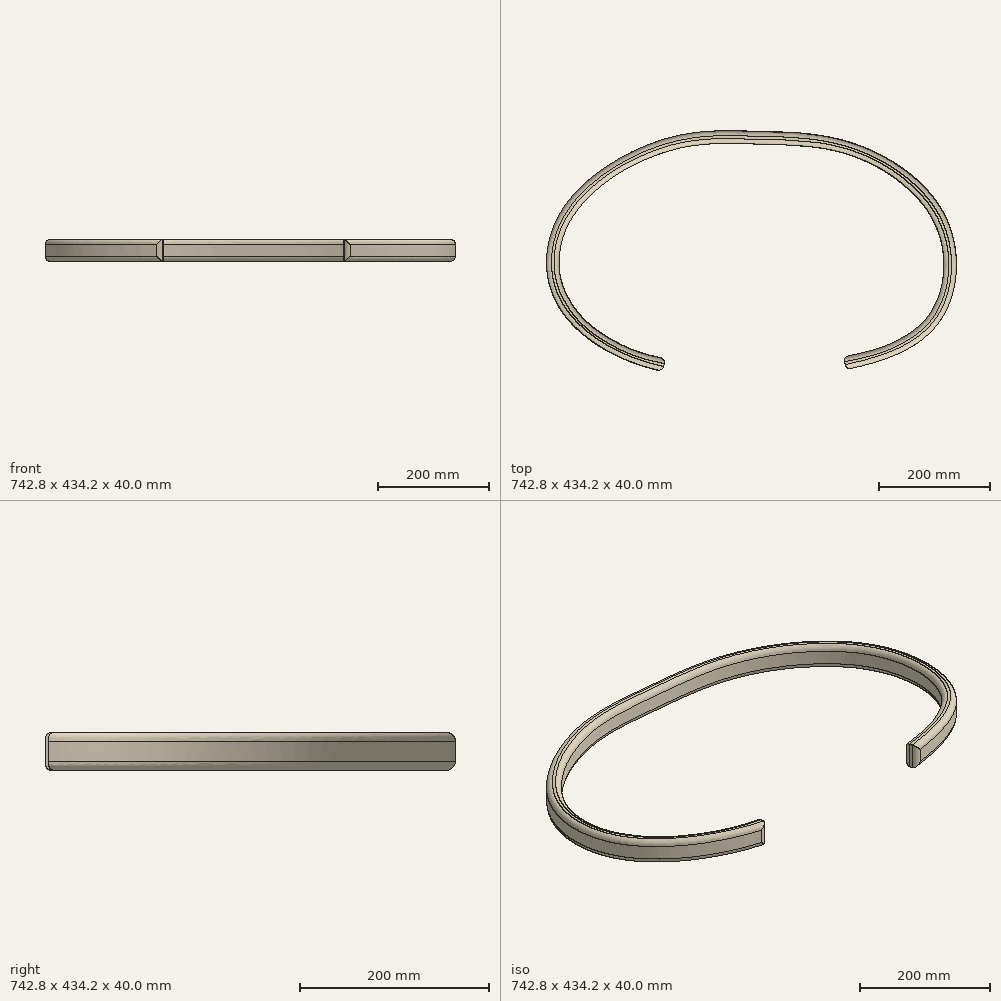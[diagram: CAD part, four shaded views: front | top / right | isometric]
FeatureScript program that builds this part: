
annotation { "Feature Type Name" : "Feature", "Feature Type Description" : "" }
export const myFeature = defineFeature(function(context is Context, id is Id, definition is map)
    precondition{}
    {
        {
            var Q0;
            Q0=qCreatedBy(makeId("Top.planeOp"),FACE);
            var sketch = newSketch(context, id + "F0", { "sketchPlane" : qUnion([Q0])});
            skFitSpline(sketch, "E0", {"points": [v(-17, -21.2) * mm, v(-36.27, -8.78) * mm, v(-35.03, 8.3) * mm, v(-16.08, 21.05) * mm, v(0, 22.29) * mm, v(17.47, 20.11) * mm, v(34.25, 6.76) * mm, v(33.63, -11.57) * mm, v(16.23, -20.9) * mm], "startDerivative": vector(-181.33, 36.59) * mm, "endDerivative": vector(-190.97, -38.94) * mm});
            skFitSpline(sketch, "E1.0", {"points": [v(-16.55, -18.92) * mm, v(-18.31, -18.56) * mm, v(-21.8, -17.56) * mm, v(-26.62, -15.27) * mm, v(-30.69, -12.34) * mm, v(-32.94, -9.8) * mm, v(-34.04, -8.02) * mm, v(-34.67, -6.82) * mm, v(-35.26, -5.25) * mm, v(-35.67, -3.3) * mm, v(-35.8, -1.3) * mm, v(-35.62, 0.72) * mm, v(-35.16, 2.74) * mm, v(-34.4, 4.73) * mm, v(-33.54, 6.35) * mm, v(-32.7, 7.6) * mm, v(-31.77, 8.82) * mm, v(-30.42, 10.3) * mm, v(-28.57, 11.99) * mm, v(-25.84, 14.07) * mm, v(-22.82, 15.86) * mm, v(-19.71, 17.32) * mm, v(-17.39, 18.22) * mm, v(-15.13, 18.92) * mm, v(-12.97, 19.43) * mm, v(-10.87, 19.76) * mm, v(-8.8, 19.96) * mm, v(-6.74, 20.06) * mm, v(-4.66, 20.07) * mm, v(-2.56, 20.03) * mm, v(-0.76, 19.98) * mm, v(0.7, 19.94) * mm, v(2.17, 19.9) * mm, v(4, 19.86) * mm, v(6.2, 19.76) * mm, v(9.14, 19.54) * mm, v(12.82, 19.04) * mm, v(17.24, 17.86) * mm, v(21.75, 15.89) * mm, v(25.26, 13.65) * mm, v(27.76, 11.56) * mm, v(29.43, 9.86) * mm, v(30.87, 8.03) * mm, v(31.84, 6.42) * mm, v(32.47, 5.08) * mm, v(33.01, 3.69) * mm, v(33.52, 1.89) * mm, v(33.85, -0.34) * mm, v(33.91, -2.57) * mm, v(33.7, -4.75) * mm, v(33.25, -6.83) * mm, v(32.66, -8.44) * mm, v(32.09, -9.62) * mm, v(31.44, -10.72) * mm, v(30.5, -11.96) * mm, v(29.14, -13.29) * mm, v(27.53, -14.47) * mm, v(25.04, -15.88) * mm, v(21.3, -17.33) * mm, v(17.7, -18.22) * mm, v(15.77, -18.61) * mm]});
            skLineSegment(sketch, "E2", {"start": v(-17, -21.2) * mm, "end": v(-16.55, -18.92) * mm});
            skLineSegment(sketch, "E3", {"start": v(15.77, -18.61) * mm, "end": v(16.23, -20.9) * mm});
            skSolve(sketch);
        }
        {
            var Q0;
            Q0 = qSketchRegion(id + "F0", true);
            extrude(context, id + "F1", {"entities" : qUnion([Q0]), "depth" : 4 * mm, "offsetDistance" : 25 * mm});
        }
        {
            var Q0;
            Q0=makeQuery(id+"F1.opExtrude","SWEPT_FACE",FACE,{"disambiguationData":[OSD([sQuery(id+"F0.wireOp",EDGE,"E0")])]});
            var Q1;
            Q1=makeQuery(id+"F1.opExtrude","SWEPT_FACE",FACE,{"disambiguationData":[OSD([sQuery(id+"F0.wireOp",EDGE,"E1.0")])]});
            fillet(context, id + "F2", {"entities" : qUnion([Q0, Q1]), "radius" : .9 * mm, "tangentPropagation" : true, "allowEdgeOverflow" : false});
        }
        {
            var Q0;
            Q0=makeQuery(id+"F1.opExtrude","SWEPT_BODY",BODY,{"disambiguationData":[OSD([sQuery(id+"F0.wireOp",EDGE,"E0"),sQuery(id+"F0.wireOp",EDGE,"E1.0"),sQuery(id+"F0.wireOp",EDGE,"E2"),sQuery(id+"F0.wireOp",EDGE,"E3")])]});
            var Q1;
            Q1=qCreatedBy(makeId("Origin.pointOp"),VERTEX);
            transform(context, id + "F3", {"entities" : qUnion([Q0]), "transformType" : TransformType.SCALE_UNIFORMLY, "scale" : 10, "scalePoint" : qUnion([Q1]), "makeCopy" : false});
        }
    });
